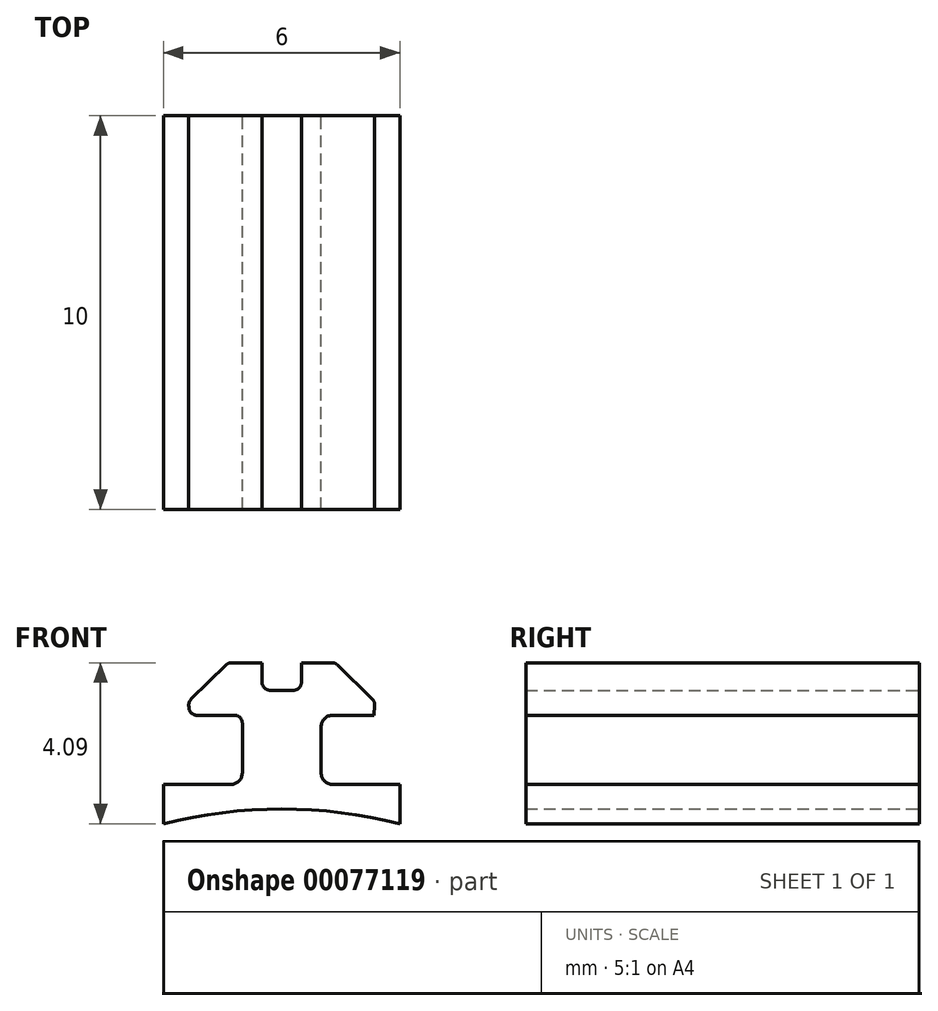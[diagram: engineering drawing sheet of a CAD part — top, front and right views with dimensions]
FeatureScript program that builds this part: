
annotation { "Feature Type Name" : "Feature", "Feature Type Description" : "" }
export const myFeature = defineFeature(function(context is Context, id is Id, definition is map)
    precondition{}
    {
        {
            var Q0;
            Q0=qCreatedBy(makeId("Front.planeOp"),FACE);
            var sketch = newSketch(context, id + "F0", { "sketchPlane" : qUnion([Q0])});
            skLineSegment(sketch, "E0", {"start": v(0, 19.4) * mm, "end": v(0, 3.26) * mm, "construction": true});
            skLineSegment(sketch, "E1", {"start": v(-3, -0.13) * mm, "end": v(-3, 0.87) * mm});
            skLineSegment(sketch, "E2", {"start": v(-3, 0.87) * mm, "end": v(-1, 0.87) * mm});
            skLineSegment(sketch, "E3", {"start": v(-1, 0.87) * mm, "end": v(-1, 2.63) * mm});
            skLineSegment(sketch, "E4", {"start": v(-1, 2.63) * mm, "end": v(-2.35, 2.63) * mm});
            skLineSegment(sketch, "E5", {"start": v(0, 3.36) * mm, "end": v(0, 3.26) * mm});
            skLineSegment(sketch, "E6.MirrorCS", {"start": v(1, 0.87) * mm, "end": v(1, 2.63) * mm});
            skLineSegment(sketch, "E7.MirrorCS", {"start": v(3, 0.87) * mm, "end": v(1, 0.87) * mm});
            skLineSegment(sketch, "E8.MirrorCS", {"start": v(3, -0.13) * mm, "end": v(3, 0.87) * mm});
            skArc(sketch, "E9", {"start": v(3, -0.13) * mm, "mid": v(0, 0.25) * mm, "end": v(-3, -0.13) * mm});
            skPoint(sketch, "E10.MirrorCS.end.orphan", {"position": v(3, -0.13) * mm});
            skPoint(sketch, "E10.MirrorCS.start.orphan", {"position": v(0, 0) * mm});
            skLineSegment(sketch, "E11", {"start": v(-1.36, 3.96) * mm, "end": v(-0.5, 3.96) * mm});
            skPoint(sketch, "E12.start.orphan", {"position": v(-2.4, 3.83) * mm});
            skLineSegment(sketch, "E13", {"start": v(-2.36, 2.98) * mm, "end": v(-1.36, 3.96) * mm});
            skPoint(sketch, "E14.orphan", {"position": v(2.4, 3.83) * mm});
            skPoint(sketch, "E15.MirrorCS.start.orphan", {"position": v(3, 2.57) * mm});
            skPoint(sketch, "E16.MirrorCS.end.orphan", {"position": v(0, 3.36) * mm});
            skLineSegment(sketch, "E17.MirrorCS", {"start": v(2.36, 2.98) * mm, "end": v(1.36, 3.96) * mm});
            skPoint(sketch, "E18.MirrorCS.start.orphan", {"position": v(1.36, 3.96) * mm});
            skLineSegment(sketch, "E19", {"start": v(-0.5, 3.96) * mm, "end": v(-0.5, 3.26) * mm});
            skLineSegment(sketch, "E20", {"start": v(-0.5, 3.26) * mm, "end": v(0, 3.26) * mm});
            skLineSegment(sketch, "E21.MirrorCS", {"start": v(0.5, 3.26) * mm, "end": v(0, 3.26) * mm});
            skLineSegment(sketch, "E22.MirrorCS", {"start": v(0.5, 3.96) * mm, "end": v(0.5, 3.26) * mm});
            skLineSegment(sketch, "E23.MirrorCS", {"start": v(1.36, 3.96) * mm, "end": v(0.5, 3.96) * mm});
            skPoint(sketch, "E24.end.orphan", {"position": v(-3, 2.57) * mm});
            skLineSegment(sketch, "E25", {"start": v(-2.36, 2.98) * mm, "end": v(-2.35, 2.63) * mm});
            skPoint(sketch, "E26.MirrorCS.start.orphan", {"position": v(1, 2.63) * mm});
            skPoint(sketch, "E27.MirrorCS.end.orphan", {"position": v(2.36, 2.98) * mm});
            skLineSegment(sketch, "E28.MirrorCS", {"start": v(1, 2.63) * mm, "end": v(2.35, 2.63) * mm});
            skLineSegment(sketch, "E29.MirrorCS", {"start": v(2.36, 2.98) * mm, "end": v(2.35, 2.63) * mm});
            skLineSegment(sketch, "E30.trimOffspring", {"start": v(0, 0.25) * mm, "end": v(0, -16.7) * mm, "construction": true});
            skLineSegment(sketch, "E31.trimOffspring", {"start": v(0, 0.25) * mm, "end": v(0, 0) * mm});
            skSolve(sketch);
        }
        {
            var Q0;
            {var subQ1=sQuery(id+"F0.wireOp",EDGE,"E1");Q0=makeQuery(id+"F0.imprint","IMPRINT",FACE,{"disambiguationData":[TD([[makeQuery(id+"F0.imprint","IMPRINT",EDGE,{"derivedFrom":subQ1}),-1.0]])]});}
            var Q1;
            Q1=makeQuery(id+"F0.imprint","IMPRINT",FACE,{"disambiguationData":[TD([[makeQuery(id+"F0.imprint","IMPRINT",EDGE,{"derivedFrom":sQuery(id+"F0.wireOp",EDGE,"E26.MirrorCS")}),1.0]])]});
            extrude(context, id + "F1", {"entities" : qUnion([Q0, Q1]), "depth" : 10 * mm});
        }
        {
            var Q0;
            Q0=makeQuery(id+"F1.opExtrude","SWEPT_EDGE",EDGE,{"disambiguationData":[OSD([sQuery(id+"F0.wireOp",EDGE,"E19"),sQuery(id+"F0.wireOp",EDGE,"E20")])]});
            var Q1;
            Q1=makeQuery(id+"F1.opExtrude","SWEPT_EDGE",EDGE,{"disambiguationData":[OSD([sQuery(id+"F0.wireOp",EDGE,"E21.MirrorCS"),sQuery(id+"F0.wireOp",EDGE,"E22.MirrorCS")])]});
            var Q2;
            Q2=makeQuery(id+"F1.opExtrude","SWEPT_EDGE",EDGE,{"disambiguationData":[OSD([sQuery(id+"F0.wireOp",EDGE,"E17.MirrorCS"),sQuery(id+"F0.wireOp",EDGE,"E27.MirrorCS")])]});
            var Q3;
            Q3=makeQuery(id+"F1.opExtrude","SWEPT_EDGE",EDGE,{"disambiguationData":[OSD([sQuery(id+"F0.wireOp",EDGE,"E26.MirrorCS"),sQuery(id+"F0.wireOp",EDGE,"E27.MirrorCS")])]});
            var Q4;
            Q4=makeQuery(id+"F1.opExtrude","SWEPT_EDGE",EDGE,{"disambiguationData":[OSD([sQuery(id+"F0.wireOp",EDGE,"Fh4L0hf9-FOak-96oc-pc29-sX1zGtYwSFka"),sQuery(id+"F0.wireOp",EDGE,"E13")])]});
            var Q5;
            Q5=makeQuery(id+"F1.opExtrude","SWEPT_EDGE",EDGE,{"disambiguationData":[OSD([sQuery(id+"F0.wireOp",EDGE,"E4"),sQuery(id+"F0.wireOp",EDGE,"Fh4L0hf9-FOak-96oc-pc29-sX1zGtYwSFka")])]});
            fillet(context, id + "F2", {"entities" : qUnion([Q0, Q1, Q2, Q3, Q4, Q5]), "radius" : .2 * mm, "tangentPropagation" : true, "allowEdgeOverflow" : false});
        }
        {
            var Q0;
            Q0=makeQuery(id+"F1.opExtrude","SWEPT_EDGE",EDGE,{"disambiguationData":[OSD([sQuery(id+"F0.wireOp",EDGE,"E3"),sQuery(id+"F0.wireOp",EDGE,"E4")])]});
            var Q1;
            Q1=makeQuery(id+"F1.opExtrude","SWEPT_EDGE",EDGE,{"disambiguationData":[OSD([sQuery(id+"F0.wireOp",EDGE,"E2"),sQuery(id+"F0.wireOp",EDGE,"E3")])]});
            var Q2;
            Q2=makeQuery(id+"F1.opExtrude","SWEPT_EDGE",EDGE,{"disambiguationData":[OSD([sQuery(id+"F0.wireOp",EDGE,"E26.MirrorCS"),sQuery(id+"F0.wireOp",EDGE,"E6.MirrorCS")])]});
            var Q3;
            Q3=makeQuery(id+"F1.opExtrude","SWEPT_EDGE",EDGE,{"disambiguationData":[OSD([sQuery(id+"F0.wireOp",EDGE,"E6.MirrorCS"),sQuery(id+"F0.wireOp",EDGE,"E7.MirrorCS")])]});
            fillet(context, id + "F3", {"entities" : qUnion([Q0, Q1, Q2, Q3]), "radius" : .3 * mm, "tangentPropagation" : true, "allowEdgeOverflow" : false});
        }
    });
